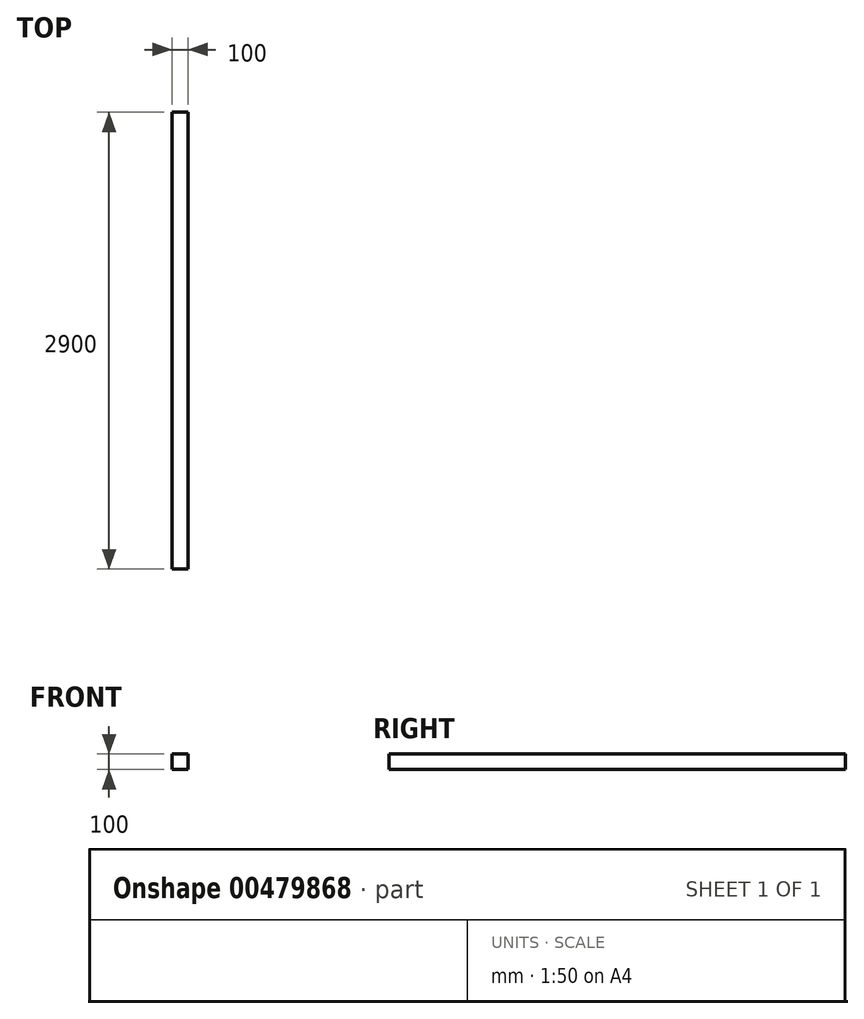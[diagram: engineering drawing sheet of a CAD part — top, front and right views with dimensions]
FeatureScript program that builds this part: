
annotation { "Feature Type Name" : "Feature", "Feature Type Description" : "" }
export const myFeature = defineFeature(function(context is Context, id is Id, definition is map)
    precondition{}
    {
        {
            var Q0;
            Q0=qCreatedBy(makeId("Right.planeOp"),FACE);
            var sketch = newSketch(context, id + "F0", { "sketchPlane" : qUnion([Q0])});
            skLineSegment(sketch, "E0", {"start": v(0, 0) * mm, "end": v(0, -100) * mm});
            skLineSegment(sketch, "E1", {"start": v(0, -100) * mm, "end": v(-2900, -100) * mm});
            skLineSegment(sketch, "E2", {"start": v(-2900, -100) * mm, "end": v(-2900, 0) * mm});
            skLineSegment(sketch, "E3", {"start": v(-2900, 0) * mm, "end": v(0, 0) * mm});
            skSolve(sketch);
        }
        {
            var Q0;
            Q0=makeQuery(id+"F0.imprint","IMPRINT",FACE,{"disambiguationData":[TD([[makeQuery(id+"F0.imprint","IMPRINT",EDGE,{"derivedFrom":sQuery(id+"F0.wireOp",EDGE,"E0")}),-1.0]])]});
            extrude(context, id + "F1", {"entities" : qUnion([Q0]), "depth" : 100 * mm});
        }
    });
